SOLIDWORKS PART (.sldprt)
format: sldprt  version: not decoded by parser v0  size: 126,976 bytes
history: native  units: mm
features: sketch x5, plane x3, extrude x3, cut_extrude x2, material x1 (+8 scaffold rows collapsed)
feature tree (22):
  scaffold x8  (default folders/planes/origin — collapsed)
  material  "Matériau <non spécifié>"
  plane  "Plan de face"
  plane  "Plan de dessus"
  plane  "Plan de droite"
  sketch  "Esquisse1"  dims[D1=~24.63688mm]
  extrude  "Extrusion1"  Depth=1.5mm
  sketch  "Esquisse2"  dims[D1=1.4mm D2=1.4mm D3=3.0mm D4=0.4mm D5=~10.113929mm]
  extrude  "Extrusion2"  Depth=5mm
  sketch  "Esquisse3"  dims[D1=~2.360259mm]
  extrude  "Extrusion3"  Depth=2mm
  sketch  "Esquisse4"  dims[c1.D1=~0.275572mm c1.D2=~1.40228mm c2.D1=1.4mm]
  cut_extrude  "Enlèv. mat.-Extru.1"  [1 undecoded]
  sketch  "Esquisse5"  dims[D1=~0.628005mm]
  cut_extrude  "Enlèv. mat.-Extru.2"  [1 undecoded]
decode coverage: 8 of 10 modeling features carry decoded parameters
note: ~ marks probable driven/reference dimensions
note: 2 parameter values undecoded
note: suppression state not decoded; provenance and decode notes live in map.json
